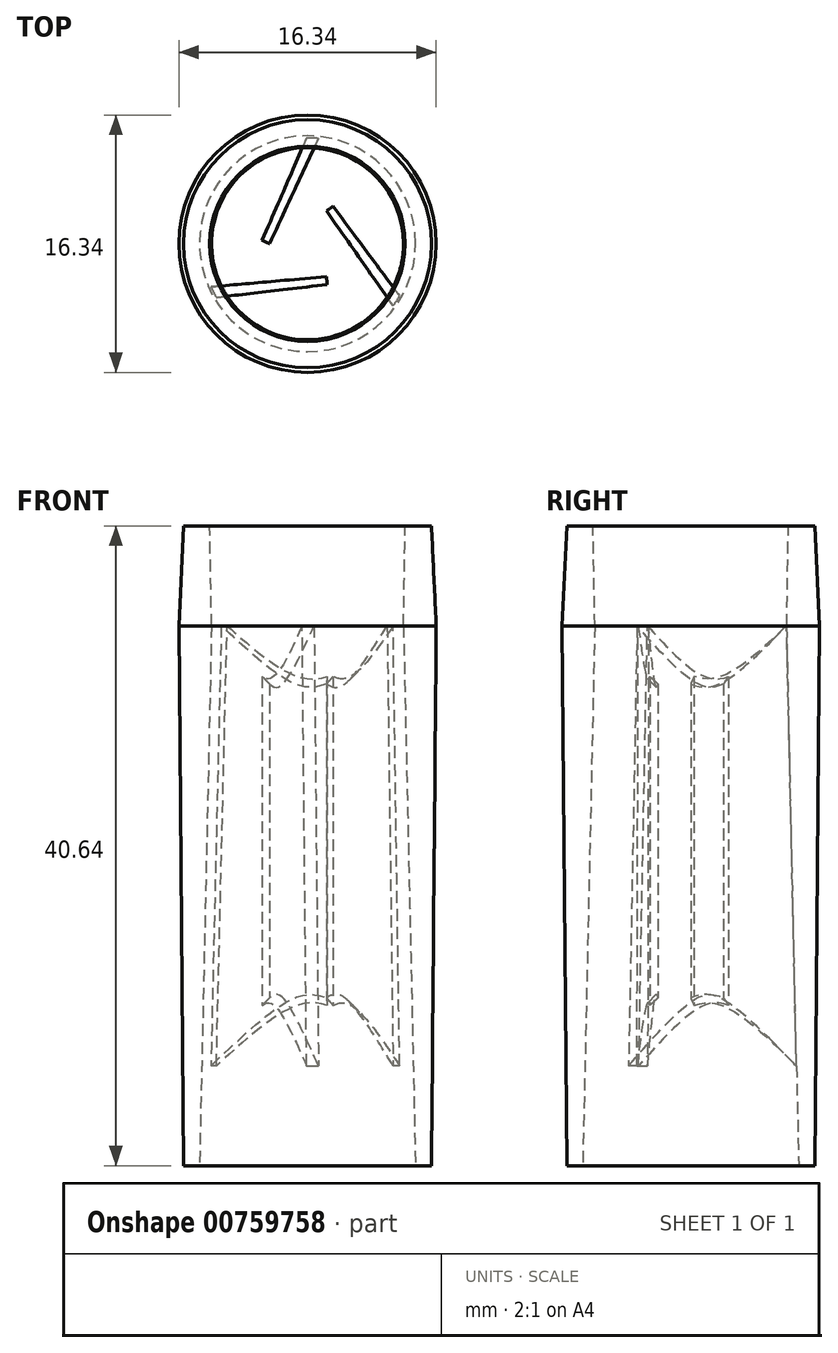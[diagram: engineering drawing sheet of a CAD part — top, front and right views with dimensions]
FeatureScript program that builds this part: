
annotation { "Feature Type Name" : "Feature", "Feature Type Description" : "" }
export const myFeature = defineFeature(function(context is Context, id is Id, definition is map)
    precondition{}
    {
        {
            var Q0;
            Q0=qCreatedBy(makeId("Front.planeOp"),FACE);
            var sketch = newSketch(context, id + "F0", { "sketchPlane" : qUnion([Q0])});
            skLineSegment(sketch, "E0", {"start": v(0, 42.55) * mm, "end": v(0, -40.36) * mm, "construction": true});
            skLineSegment(sketch, "E1", {"start": v(-34.6, 0) * mm, "end": v(27.82, 0) * mm, "construction": true});
            skLineSegment(sketch, "E2", {"start": v(6.2, 20.32) * mm, "end": v(6.1, 13.97) * mm});
            skLineSegment(sketch, "E3", {"start": v(6.1, 13.97) * mm, "end": v(6.86, -20.32) * mm});
            skLineSegment(sketch, "E4", {"start": v(6.86, -20.32) * mm, "end": v(7.87, -20.32) * mm});
            skLineSegment(sketch, "E5", {"start": v(7.87, -20.32) * mm, "end": v(8.17, 13.97) * mm});
            skLineSegment(sketch, "E6", {"start": v(7.87, 20.32) * mm, "end": v(6.2, 20.32) * mm});
            skLineSegment(sketch, "E7", {"start": v(8.17, 13.97) * mm, "end": v(3.33, 13.97) * mm, "construction": true});
            skLineSegment(sketch, "E8", {"start": v(8.17, 13.97) * mm, "end": v(7.87, 20.32) * mm});
            skSolve(sketch);
        }
        {
            var Q0;
            Q0=makeQuery(id+"F0.imprint","IMPRINT",FACE,{"disambiguationData":[TD([[makeQuery(id+"F0.imprint","IMPRINT",EDGE,{"derivedFrom":sQuery(id+"F0.wireOp",EDGE,"E2")}),1.0]])]});
            var Q1;
            Q1=sQuery(id+"F0.wireOp",EDGE,"E0");
            revolve(context, id + "F1", {"entities" : qUnion([Q0]), "axis" : qUnion([Q1]), "revolveType" : RevolveType.FULL});
        }
        {
            var Q0;
            Q0=makeQuery(id+"F1.opRevolve","SWEPT_FACE",FACE,{"disambiguationData":[OSD([sQuery(id+"F0.wireOp",EDGE,"E4")])]});
            var sketch = newSketch(context, id + "F2", { "sketchPlane" : qUnion([Q0])});
            skCircle(sketch, "E9.0", {"center": v(0, 0) * mm, "radius": 6.86 * mm});
            skCircle(sketch, "E10", {"center": v(0, 0) * mm, "radius": 2.41 * mm, "construction": true});
            skLineSegment(sketch, "E11", {"start": v(0.76, -6.82) * mm, "end": v(-2.41, 0) * mm});
            skLineSegment(sketch, "E12", {"start": v(-2.41, 0) * mm, "end": v(-2.87, -0.21) * mm});
            skLineSegment(sketch, "E13", {"start": v(-2.87, -0.21) * mm, "end": v(0, -6.86) * mm});
            skLineSegment(sketch, "E14.1.0", {"start": v(1.2, -2.09) * mm, "end": v(1.62, -2.38) * mm});
            skLineSegment(sketch, "E14.1.1", {"start": v(1.62, -2.38) * mm, "end": v(5.94, 3.43) * mm});
            skLineSegment(sketch, "E14.1.2", {"start": v(5.52, 4.07) * mm, "end": v(1.2, -2.09) * mm});
            skLineSegment(sketch, "E14.2.0", {"start": v(1.2, 2.09) * mm, "end": v(1.25, 2.6) * mm});
            skLineSegment(sketch, "E14.2.1", {"start": v(1.25, 2.6) * mm, "end": v(-5.94, 3.43) * mm});
            skLineSegment(sketch, "E14.2.2", {"start": v(-6.28, 2.75) * mm, "end": v(1.2, 2.09) * mm});
            skSolve(sketch);
        }
        {
            var Q0;
            Q0=makeQuery(id+"F2.imprint","IMPRINT",FACE,{"disambiguationData":[TD([[makeQuery(id+"F2.imprint","IMPRINT",EDGE,{"derivedFrom":sQuery(id+"F2.wireOp",EDGE,"E14.2.0")}),1.0]])]});
            var Q1;
            {var subQ0=sQuery(id+"F2.wireOp",EDGE,"E11");Q1=makeQuery(id+"F2.imprint","IMPRINT",FACE,{"disambiguationData":[TD([[makeQuery(id+"F2.imprint","IMPRINT",EDGE,{"derivedFrom":subQ0}),1.0]])]});}
            var Q2;
            Q2=makeQuery(id+"F2.imprint","IMPRINT",FACE,{"disambiguationData":[TD([[makeQuery(id+"F2.imprint","IMPRINT",EDGE,{"derivedFrom":sQuery(id+"F2.wireOp",EDGE,"E14.1.0")}),1.0]])]});
            extrude(context, id + "F3", {"entities" : qUnion([Q0, Q1, Q2]), "operationType" : NewBodyOperationType.ADD, "oppositeDirection" : true, "depth" : 34.3 * mm, "offsetDistance" : 25.4 * mm});
        }
        {
            var Q0;
            Q0=qCreatedBy(makeId("Front.planeOp"),FACE);
            var sketch = newSketch(context, id + "F4", { "sketchPlane" : qUnion([Q0])});
            skPoint(sketch, "E15.0", {"position": v(6.86, -20.32) * mm});
            skPoint(sketch, "E16.0", {"position": v(6.1, 13.97) * mm});
            skLineSegment(sketch, "E17.0", {"start": v(6.1, 13.97) * mm, "end": v(6.86, -20.32) * mm});
            skLineSegment(sketch, "E18", {"start": v(6.86, -20.32) * mm, "end": v(6.72, -13.97) * mm});
            skLineSegment(sketch, "E19", {"start": v(6.72, -13.97) * mm, "end": v(0, -7.25) * mm});
            skLineSegment(sketch, "E20", {"start": v(0, -7.25) * mm, "end": v(0, -20.47) * mm});
            skLineSegment(sketch, "E21", {"start": v(0, -20.47) * mm, "end": v(6.86, -20.32) * mm});
            skLineSegment(sketch, "E22", {"start": v(6.1, 13.97) * mm, "end": v(0, 13.97) * mm});
            skLineSegment(sketch, "E23", {"start": v(0, 13.97) * mm, "end": v(0, 7.87) * mm});
            skLineSegment(sketch, "E24", {"start": v(0, 7.87) * mm, "end": v(6.1, 13.97) * mm});
            skSolve(sketch);
        }
        {
            var Q0;
            Q0=makeQuery(id+"F4.imprint","IMPRINT",FACE,{"disambiguationData":[TD([[makeQuery(id+"F4.imprint","IMPRINT",EDGE,{"derivedFrom":sQuery(id+"F4.wireOp",EDGE,"E22")}),1.0]])]});
            var Q1;
            {var subQ2=sQuery(id+"F4.wireOp",EDGE,"E19");Q1=makeQuery(id+"F4.imprint","IMPRINT",FACE,{"disambiguationData":[TD([[makeQuery(id+"F4.imprint","IMPRINT",EDGE,{"derivedFrom":subQ2}),1.0]])]});}
            var Q2;
            Q2=sQuery(id+"F0.wireOp",EDGE,"E0");
            revolve(context, id + "F5", {"operationType" : NewBodyOperationType.REMOVE, "entities" : qUnion([Q0, Q1]), "axis" : qUnion([Q2]), "revolveType" : RevolveType.FULL, "oppositeDirection" : true});
        }
    });
